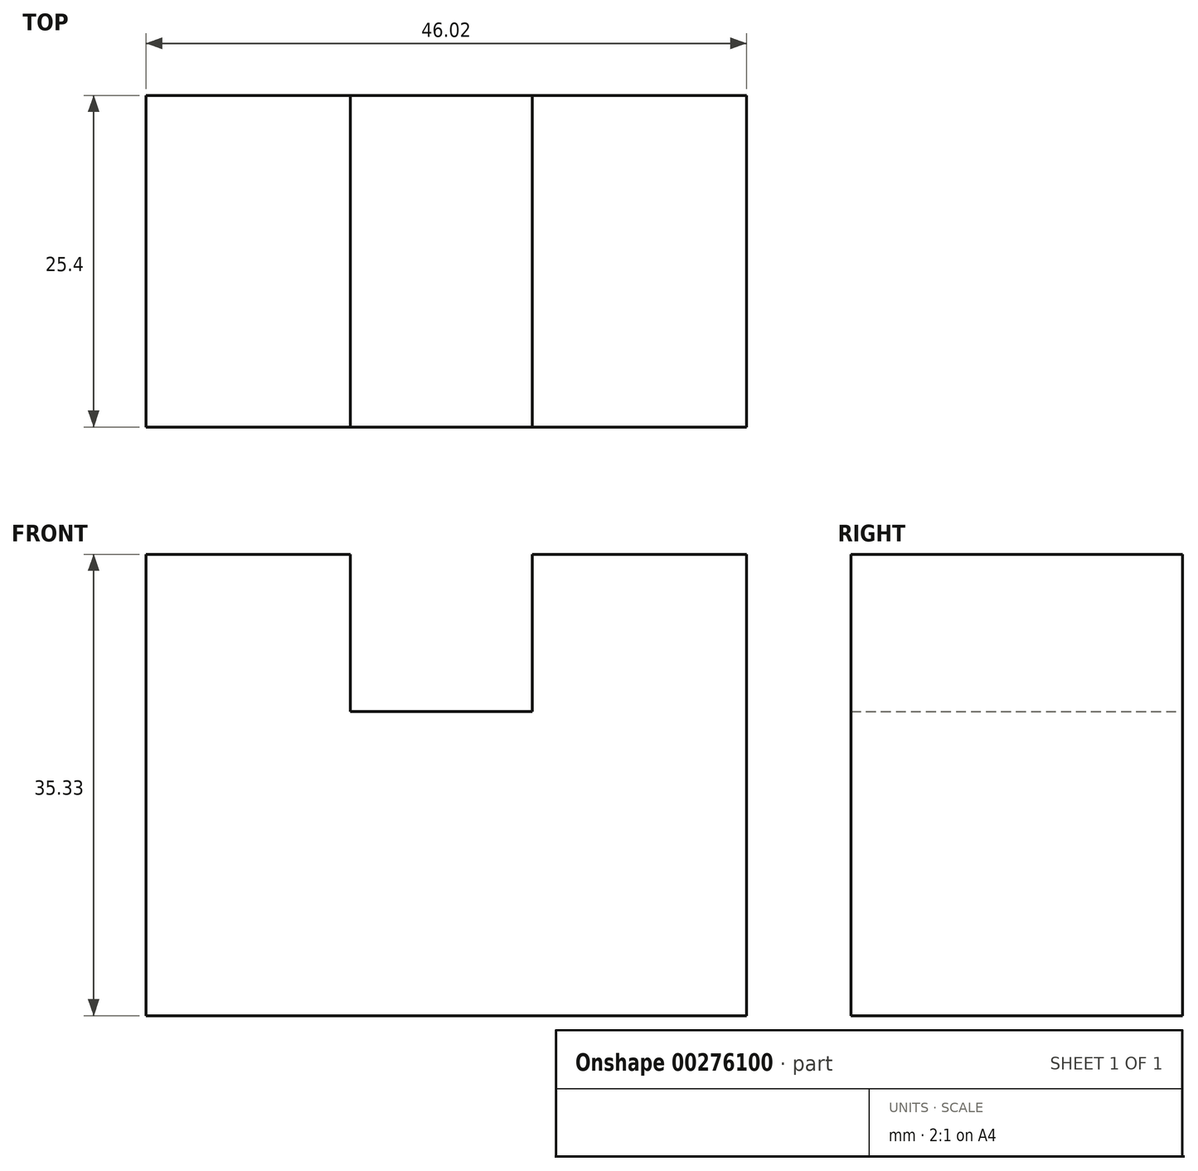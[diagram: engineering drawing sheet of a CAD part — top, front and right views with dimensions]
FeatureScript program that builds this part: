
annotation { "Feature Type Name" : "Feature", "Feature Type Description" : "" }
export const myFeature = defineFeature(function(context is Context, id is Id, definition is map)
    precondition{}
    {
        {
            var Q0;
            Q0=qCreatedBy(makeId("Front.planeOp"),FACE);
            var sketch = newSketch(context, id + "F0", { "sketchPlane" : qUnion([Q0])});
            skLineSegment(sketch, "E0", {"start": v(0, 0) * mm, "end": v(-46.02, 0) * mm});
            skLineSegment(sketch, "E1", {"start": v(-46.02, 0) * mm, "end": v(-46.02, 35.33) * mm});
            skLineSegment(sketch, "E2", {"start": v(-46.02, 35.33) * mm, "end": v(-30.36, 35.33) * mm});
            skLineSegment(sketch, "E3", {"start": v(-30.36, 35.33) * mm, "end": v(-30.36, 23.3) * mm});
            skLineSegment(sketch, "E4", {"start": v(-30.36, 23.3) * mm, "end": v(-16.42, 23.3) * mm});
            skLineSegment(sketch, "E5", {"start": v(-16.42, 23.3) * mm, "end": v(-16.42, 35.33) * mm});
            skLineSegment(sketch, "E6", {"start": v(-16.42, 35.33) * mm, "end": v(0, 35.33) * mm});
            skLineSegment(sketch, "E7", {"start": v(0, 35.33) * mm, "end": v(0, 0) * mm});
            skSolve(sketch);
        }
        {
            var Q0;
            Q0 = qSketchRegion(id + "F0", true);
            extrude(context, id + "F1", {"entities" : qUnion([Q0]), "depth" : 25.4 * mm});
        }
    });
